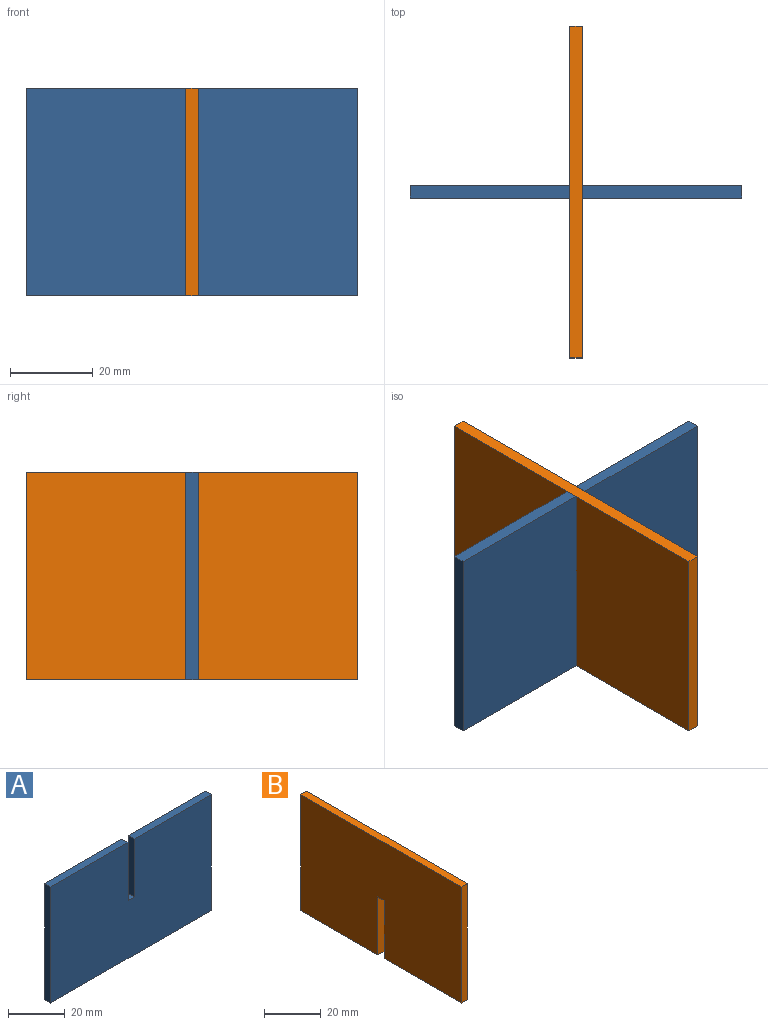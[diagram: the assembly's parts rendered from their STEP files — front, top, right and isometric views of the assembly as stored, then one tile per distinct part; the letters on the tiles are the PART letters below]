
ASSEMBLY  parts=2 mates=1
PART A: 10 faces, bbox 80x3x50 mm
  f0: plane 50x3mm, normal (1,0,0), area 150mm2, adj f1,f7,f8,f9
  f1: plane 38.5x3mm, normal (0,0,1), area 115.5mm2, adj f0,f2,f8,f9
  f2: plane 25x3mm, normal (-1,0,0), area 75mm2, adj f1,f3,f8,f9
  f3: plane 3x3mm, normal (0,0,1), area 9mm2, adj f2,f4,f8,f9
  f4: plane 25x3mm, normal (1,0,0), area 75mm2, adj f3,f5,f8,f9
  f5: plane 38.5x3mm, normal (0,0,1), area 115.5mm2, adj f4,f6,f8,f9
  f6: plane 50x3mm, normal (-1,0,0), area 150mm2, adj f5,f7,f8,f9
  f7: plane 80x3mm, normal (0,0,-1), area 240mm2, adj f0,f6,f8,f9
  f8: plane 80x50mm, normal (0,-1,0), area 3925mm2, adj f0,f1,f2,f3,f4,f5,f6,f7
  f9: plane 80x50mm, normal (0,1,0), area 3925mm2, adj f0,f1,f2,f3,f4,f5,f6,f7
PART B: 10 faces, bbox 3x80x50 mm
  f0: plane 38.5x3mm, normal (0,0,-1), area 115.5mm2, adj f2,f5,f6,f8
  f1: plane 38.5x3mm, normal (0,0,-1), area 115.5mm2, adj f4,f5,f6,f7
  f2: plane 50x3mm, normal (0,1,0), area 150mm2, adj f0,f3,f5,f6
  f3: plane 80x3mm, normal (0,0,1), area 240mm2, adj f2,f4,f5,f6
  f4: plane 50x3mm, normal (0,-1,0), area 150mm2, adj f1,f3,f5,f6
  f5: plane 80x50mm, normal (1,0,0), area 3925mm2, adj f0,f1,f2,f3,f4,f7,f8,f9
  f6: plane 80x50mm, normal (-1,0,0), area 3925mm2, adj f0,f1,f2,f3,f4,f7,f8,f9
  f7: plane 25x3mm, normal (0,1,0), area 75mm2, adj f1,f5,f6,f9
  f8: plane 25x3mm, normal (0,-1,0), area 75mm2, adj f0,f5,f6,f9
  f9: plane 3x3mm, normal (0,0,-1), area 9mm2, adj f5,f6,f7,f8
PLACE A t=(6.88,28.75,31.47)mm
PLACE B t=(6.88,28.75,31.47)mm
MATE fastened A.f3 <-> B.f9  axis (0,0,1) through (6.88,28.75,56.47)mm
